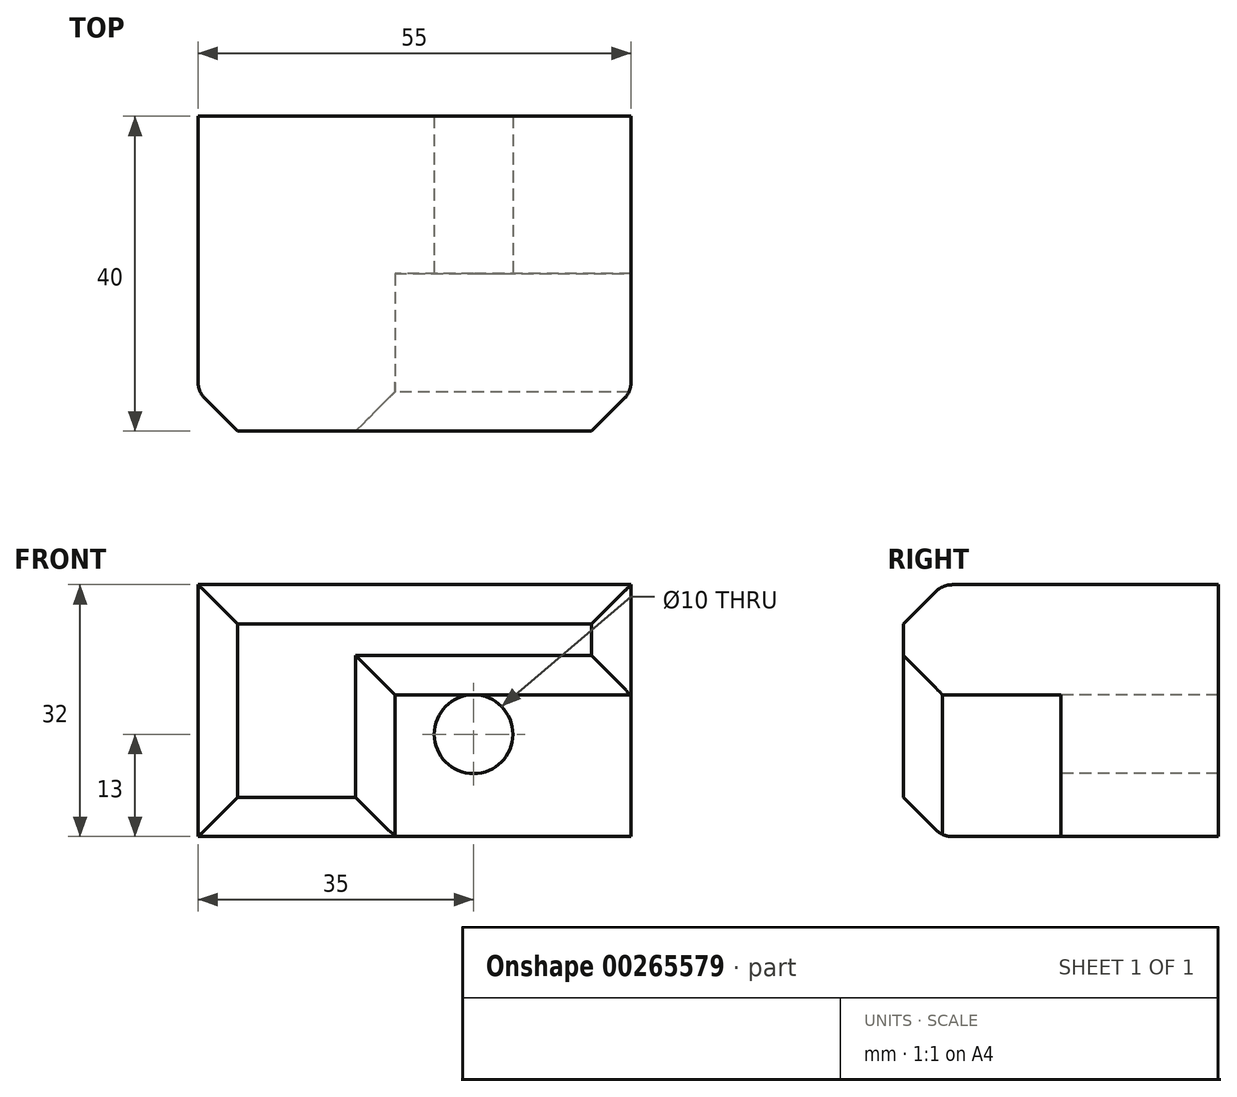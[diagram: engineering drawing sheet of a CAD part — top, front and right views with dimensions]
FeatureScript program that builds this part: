
annotation { "Feature Type Name" : "Feature", "Feature Type Description" : "" }
export const myFeature = defineFeature(function(context is Context, id is Id, definition is map)
    precondition{}
    {
        {
            var Q0;
            Q0=qCreatedBy(makeId("Front.planeOp"),FACE);
            var sketch = newSketch(context, id + "F0", { "sketchPlane" : qUnion([Q0])});
            skLineSegment(sketch, "E0.bottom", {"start": v(0, 0) * mm, "end": v(55, 0) * mm});
            skLineSegment(sketch, "E0.top", {"start": v(0, -32) * mm, "end": v(55, -32) * mm});
            skLineSegment(sketch, "E0.left", {"start": v(0, 0) * mm, "end": v(0, -32) * mm});
            skLineSegment(sketch, "E0.right", {"start": v(55, 0) * mm, "end": v(55, -32) * mm});
            skSolve(sketch);
        }
        {
            var Q0;
            Q0 = qSketchRegion(id + "F0", true);
            extrude(context, id + "F1", {"entities" : qUnion([Q0]), "depth" : 40 * mm});
        }
        {
            var Q0;
            Q0=qCreatedBy(makeId("Front.planeOp"),FACE);
            var sketch = newSketch(context, id + "F2", { "sketchPlane" : qUnion([Q0])});
            skLineSegment(sketch, "E1.bottom", {"start": v(50.86, -29.24) * mm, "end": v(20.86, -29.24) * mm});
            skLineSegment(sketch, "E1.top", {"start": v(50.86, -11.24) * mm, "end": v(20.86, -11.24) * mm});
            skLineSegment(sketch, "E1.left", {"start": v(50.86, -29.24) * mm, "end": v(50.86, -11.24) * mm});
            skLineSegment(sketch, "E1.right", {"start": v(20.86, -29.24) * mm, "end": v(20.86, -11.24) * mm});
            skSolve(sketch);
        }
        {
            var Q0;
            Q0 = qSketchRegion(id + "F2", true);
            extrude(context, id + "F3", {"entities" : qUnion([Q0]), "operationType" : NewBodyOperationType.REMOVE, "oppositeDirection" : true, "depth" : 20 * mm});
        }
        {
            var Q0;
            Q0=makeQuery(id+"F1.opExtrude","CAP_FACE",FACE,{"disambiguationData":[OSD([sQuery(id+"F0.wireOp",EDGE,"E0.bottom"),sQuery(id+"F0.wireOp",EDGE,"E0.top"),sQuery(id+"F0.wireOp",EDGE,"E0.left"),sQuery(id+"F0.wireOp",EDGE,"E0.right")])],"isStart":false});
            var sketch = newSketch(context, id + "F4", { "sketchPlane" : qUnion([Q0])});
            skLineSegment(sketch, "E2.bottom", {"start": v(55, -32) * mm, "end": v(25, -32) * mm});
            skLineSegment(sketch, "E2.top", {"start": v(55, -14) * mm, "end": v(25, -14) * mm});
            skLineSegment(sketch, "E2.left", {"start": v(55, -32) * mm, "end": v(55, -14) * mm});
            skLineSegment(sketch, "E2.right", {"start": v(25, -32) * mm, "end": v(25, -14) * mm});
            skSolve(sketch);
        }
        {
            var Q0;
            Q0 = qSketchRegion(id + "F4", true);
            extrude(context, id + "F5", {"entities" : qUnion([Q0]), "operationType" : NewBodyOperationType.REMOVE, "oppositeDirection" : true, "depth" : 20 * mm});
        }
        {
            var Q0;
            Q0=makeQuery(id+"F5.boolean.opBoolean","COPY",FACE,{"derivedFrom":makeQuery(id+"F5.opExtrude","CAP_FACE",FACE,{"disambiguationData":[OSD([sQuery(id+"F4.wireOp",EDGE,"E2.bottom"),sQuery(id+"F4.wireOp",EDGE,"E2.top"),sQuery(id+"F4.wireOp",EDGE,"E2.left"),sQuery(id+"F4.wireOp",EDGE,"E2.right")])],"isStart":false})});
            var sketch = newSketch(context, id + "F6", { "sketchPlane" : qUnion([Q0])});
            skCircle(sketch, "E3", {"center": v(35, -19) * mm, "radius": 5 * mm});
            skSolve(sketch);
        }
        {
            var Q0;
            Q0 = qSketchRegion(id + "F6", true);
            extrude(context, id + "F7", {"entities" : qUnion([Q0]), "operationType" : NewBodyOperationType.REMOVE, "endBound" : BoundingType.THROUGH_ALL, "oppositeDirection" : true, "depth" : 25 * mm});
        }
        {
            var Q0;
            Q0=makeQuery(id+"F1.opExtrude","CAP_EDGE",EDGE,{"disambiguationData":[OSD([sQuery(id+"F0.wireOp",EDGE,"E0.top")])],"isStart":false});
            var Q1;
            Q1=makeQuery(id+"F5.boolean.opBoolean","COPY",EDGE,{"derivedFrom":makeQuery(id+"F5.opExtrude","CAP_EDGE",EDGE,{"disambiguationData":[OSD([sQuery(id+"F4.wireOp",EDGE,"E2.right")])],"isStart":true})});
            var Q2;
            Q2=makeQuery(id+"F5.boolean.opBoolean","COPY",EDGE,{"derivedFrom":makeQuery(id+"F5.opExtrude","CAP_EDGE",EDGE,{"disambiguationData":[OSD([sQuery(id+"F4.wireOp",EDGE,"E2.top")])],"isStart":true})});
            var Q3;
            Q3=makeQuery(id+"F1.opExtrude","CAP_EDGE",EDGE,{"disambiguationData":[OSD([sQuery(id+"F0.wireOp",EDGE,"E0.right")])],"isStart":false});
            var Q4;
            Q4=makeQuery(id+"F1.opExtrude","CAP_FACE",FACE,{"disambiguationData":[OSD([sQuery(id+"F0.wireOp",EDGE,"E0.bottom"),sQuery(id+"F0.wireOp",EDGE,"E0.top"),sQuery(id+"F0.wireOp",EDGE,"E0.left"),sQuery(id+"F0.wireOp",EDGE,"E0.right")])],"isStart":false});
            chamfer(context, id + "F8", {"entities" : qUnion([Q0, Q1, Q2, Q3, Q4]), "width" : 5 * mm, "tangentPropagation" : true});
        }
        {
            var Q0;
            {var subQ0=sQuery(id+"F0.wireOp",EDGE,"E0.left");Q0=makeQuery(id+"F8.opChamfer","BLEND_EDGE",EDGE,{"blendedFrom":[makeQuery(id+"F1.opExtrude","CAP_EDGE",EDGE,{"disambiguationData":[OSD([subQ0])],"isStart":false}),makeQuery(id+"F1.opExtrude","SWEPT_FACE",FACE,{"disambiguationData":[OSD([subQ0])]})],"blendedInto":[makeQuery(id+"F1.opExtrude","SWEPT_FACE",FACE,{"disambiguationData":[OSD([subQ0])]})]});}
            var Q1;
            {var subQ0=sQuery(id+"F0.wireOp",EDGE,"E0.top");Q1=makeQuery(id+"F8.opChamfer","BLEND_EDGE",EDGE,{"blendedFrom":[makeQuery(id+"F1.opExtrude","CAP_EDGE",EDGE,{"disambiguationData":[OSD([subQ0])],"isStart":false}),makeQuery(id+"F1.opExtrude","SWEPT_FACE",FACE,{"disambiguationData":[OSD([subQ0])]})],"blendedInto":[makeQuery(id+"F1.opExtrude","SWEPT_FACE",FACE,{"disambiguationData":[OSD([subQ0])]})]});}
            var Q2;
            {var subQ0=sQuery(id+"F4.wireOp",EDGE,"E2.right");Q2=makeQuery(id+"F8.opChamfer","BLEND_EDGE",EDGE,{"blendedFrom":[makeQuery(id+"F5.boolean.opBoolean","COPY",EDGE,{"derivedFrom":makeQuery(id+"F5.opExtrude","CAP_EDGE",EDGE,{"disambiguationData":[OSD([subQ0])],"isStart":true})}),makeQuery(id+"F5.boolean.opBoolean","COPY",FACE,{"derivedFrom":makeQuery(id+"F5.opExtrude","SWEPT_FACE",FACE,{"disambiguationData":[OSD([subQ0])]})})],"blendedInto":[makeQuery(id+"F5.boolean.opBoolean","COPY",FACE,{"derivedFrom":makeQuery(id+"F5.opExtrude","SWEPT_FACE",FACE,{"disambiguationData":[OSD([subQ0])]})})]});}
            var Q3;
            {var subQ0=sQuery(id+"F4.wireOp",EDGE,"E2.top");Q3=makeQuery(id+"F8.opChamfer","BLEND_EDGE",EDGE,{"blendedFrom":[makeQuery(id+"F5.boolean.opBoolean","COPY",EDGE,{"derivedFrom":makeQuery(id+"F5.opExtrude","CAP_EDGE",EDGE,{"disambiguationData":[OSD([subQ0])],"isStart":true})}),makeQuery(id+"F5.boolean.opBoolean","COPY",FACE,{"derivedFrom":makeQuery(id+"F5.opExtrude","SWEPT_FACE",FACE,{"disambiguationData":[OSD([subQ0])]})})],"blendedInto":[makeQuery(id+"F5.boolean.opBoolean","COPY",FACE,{"derivedFrom":makeQuery(id+"F5.opExtrude","SWEPT_FACE",FACE,{"disambiguationData":[OSD([subQ0])]})})]});}
            var Q4;
            {var subQ0=sQuery(id+"F0.wireOp",EDGE,"E0.right");Q4=makeQuery(id+"F8.opChamfer","BLEND_EDGE",EDGE,{"blendedFrom":[makeQuery(id+"F1.opExtrude","CAP_EDGE",EDGE,{"disambiguationData":[OSD([subQ0])],"isStart":false}),makeQuery(id+"F1.opExtrude","SWEPT_FACE",FACE,{"disambiguationData":[OSD([subQ0])]})],"blendedInto":[makeQuery(id+"F1.opExtrude","SWEPT_FACE",FACE,{"disambiguationData":[OSD([subQ0])]})]});}
            var Q5;
            {var subQ0=sQuery(id+"F0.wireOp",EDGE,"E0.bottom");Q5=makeQuery(id+"F8.opChamfer","BLEND_EDGE",EDGE,{"blendedFrom":[makeQuery(id+"F1.opExtrude","CAP_EDGE",EDGE,{"disambiguationData":[OSD([subQ0])],"isStart":false}),makeQuery(id+"F1.opExtrude","SWEPT_FACE",FACE,{"disambiguationData":[OSD([subQ0])]})],"blendedInto":[makeQuery(id+"F1.opExtrude","SWEPT_FACE",FACE,{"disambiguationData":[OSD([subQ0])]})]});}
            fillet(context, id + "F9", {"entities" : qUnion([Q0, Q1, Q2, Q3, Q4, Q5]), "radius" : 3 * mm, "tangentPropagation" : true, "allowEdgeOverflow" : false});
        }
    });
